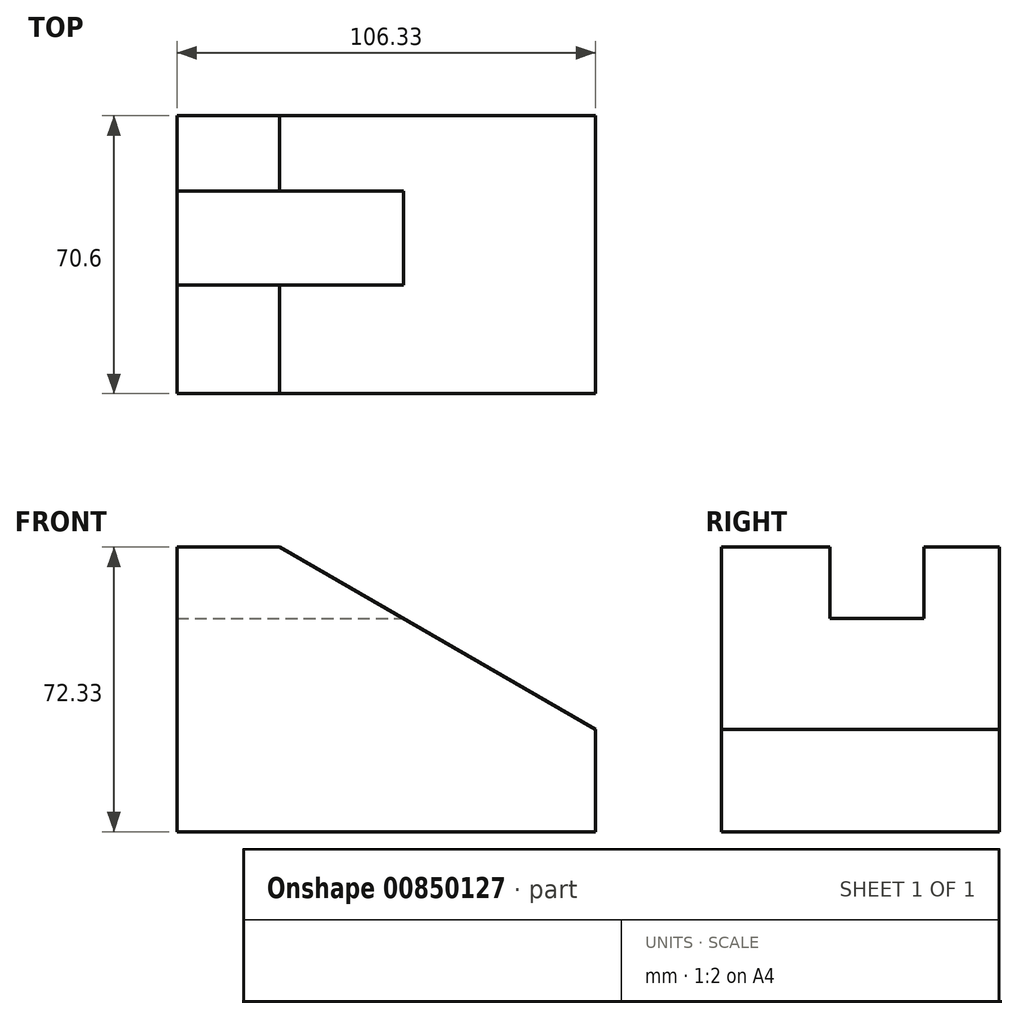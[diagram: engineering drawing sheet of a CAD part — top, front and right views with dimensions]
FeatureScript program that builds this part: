
annotation { "Feature Type Name" : "Feature", "Feature Type Description" : "" }
export const myFeature = defineFeature(function(context is Context, id is Id, definition is map)
    precondition{}
    {
        {
            var Q0;
            Q0=qCreatedBy(makeId("Front.planeOp"),FACE);
            var sketch = newSketch(context, id + "F0", { "sketchPlane" : qUnion([Q0])});
            skLineSegment(sketch, "E0.bottom", {"start": v(0, 0) * mm, "end": v(106.33, 0) * mm});
            skLineSegment(sketch, "E0.top", {"start": v(0, 72.33) * mm, "end": v(106.33, 72.33) * mm});
            skLineSegment(sketch, "E0.left", {"start": v(0, 0) * mm, "end": v(0, 72.33) * mm});
            skLineSegment(sketch, "E0.right", {"start": v(106.33, 0) * mm, "end": v(106.33, 72.33) * mm});
            skLineSegment(sketch, "E1", {"start": v(18.96, 76.45) * mm, "end": v(110.45, 23.7) * mm});
            skLineSegment(sketch, "E2", {"start": v(-11.95, 54.2) * mm, "end": v(119.1, 54.2) * mm});
            skSolve(sketch);
        }
        {
            var Q0;
            {var subQ6=sQuery(id+"F0.wireOp",EDGE,"E0.bottom");Q0=makeQuery(id+"F0.imprint","IMPRINT",FACE,{"disambiguationData":[TD([[makeQuery(id+"F0.imprint","IMPRINT",EDGE,{"derivedFrom":subQ6}),1.0]])]});}
            var Q1;
            {var subQ0=sQuery(id+"F0.wireOp",EDGE,"E0.left");var subQ1=sQuery(id+"F0.wireOp",EDGE,"E0.top");var subQ2=makeQuery(id+"F0.imprint","INTERSECT",VERTEX,{"derivedFrom":[subQ1,subQ0]});Q1=makeQuery(id+"F0.imprint","IMPRINT",FACE,{"disambiguationData":[TD([[makeQuery(id+"F0.imprint","IMPRINT",EDGE,{"disambiguationData":[TD([[subQ2,-1.0]])],"derivedFrom":subQ1}),-1.0]])]});}
            extrude(context, id + "F1", {"entities" : qUnion([Q0, Q1]), "depth" : 70.6 * mm, "offsetDistance" : 25 * mm});
        }
        {
            var Q0;
            {var subQ0=sQuery(id+"F0.wireOp",EDGE,"E0.left");var subQ1=sQuery(id+"F0.wireOp",EDGE,"E0.top");var subQ2=makeQuery(id+"F0.imprint","INTERSECT",VERTEX,{"derivedFrom":[subQ1,subQ0]});Q0=makeQuery(id+"F0.imprint","IMPRINT",FACE,{"disambiguationData":[TD([[makeQuery(id+"F0.imprint","IMPRINT",EDGE,{"disambiguationData":[TD([[subQ2,-1.0]])],"derivedFrom":subQ1}),-1.0]])]});}
            extrude(context, id + "F2", {"entities" : qUnion([Q0]), "operationType" : NewBodyOperationType.REMOVE, "depth" : 43 * mm, "offsetDistance" : 25 * mm, "hasSecondDirection" : true, "secondDirectionOppositeDirection" : false, "secondDirectionDepth" : 19.1 * mm});
        }
    });
